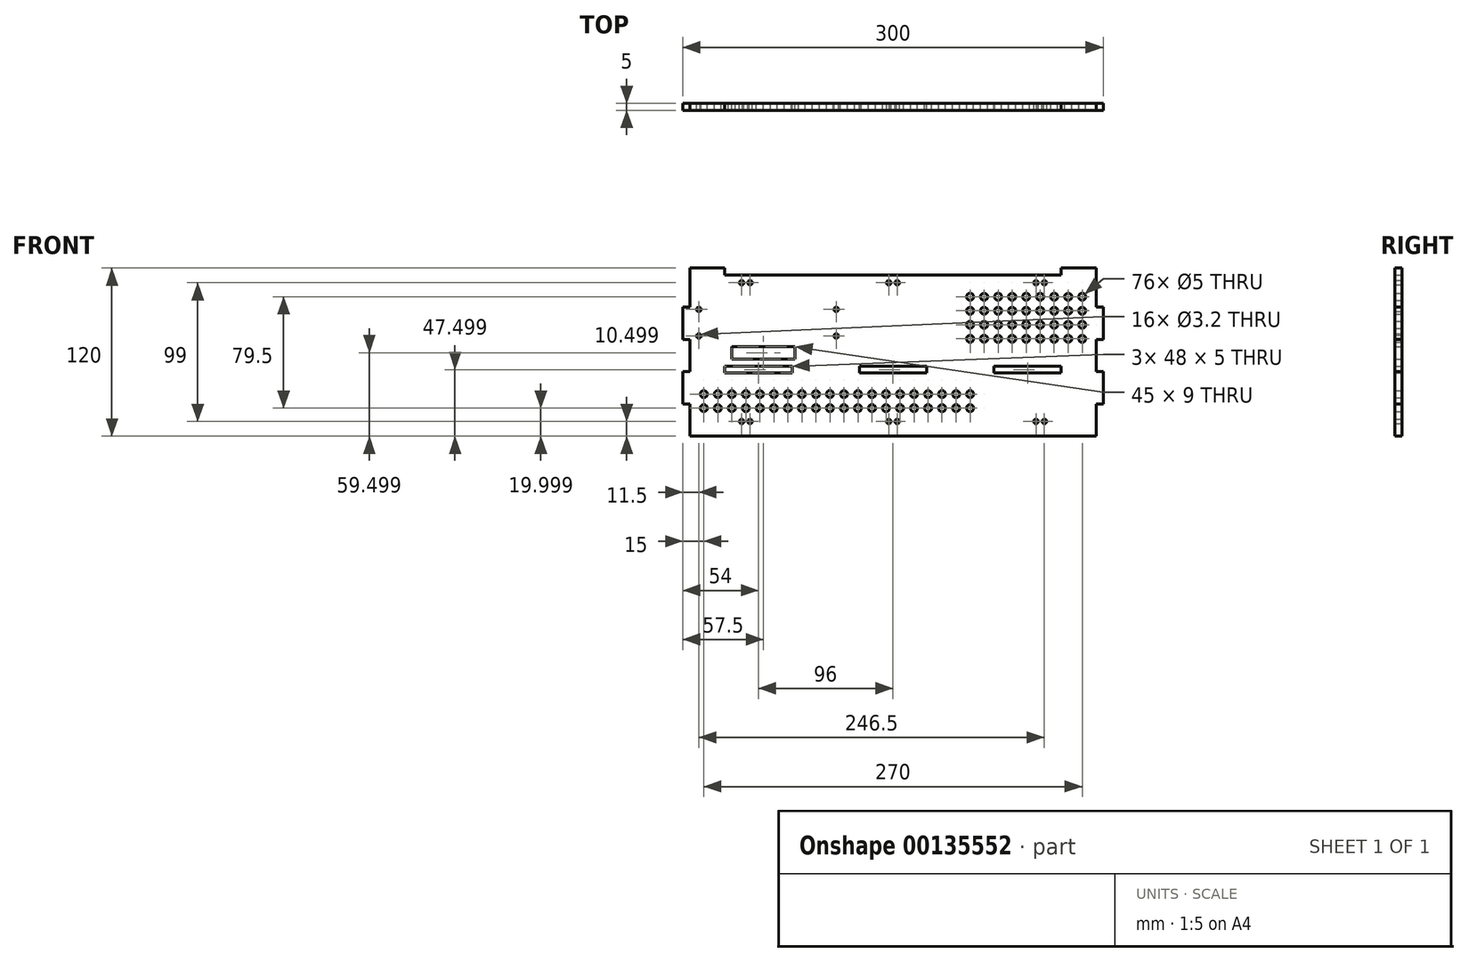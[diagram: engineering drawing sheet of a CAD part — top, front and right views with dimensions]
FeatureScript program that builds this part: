
annotation { "Feature Type Name" : "Feature", "Feature Type Description" : "" }
export const myFeature = defineFeature(function(context is Context, id is Id, definition is map)
    precondition{}
    {
        {
            var Q0;
            Q0=qCreatedBy(makeId("Front.planeOp"),FACE);
            var sketch = newSketch(context, id + "F0", { "sketchPlane" : qUnion([Q0])});
            skLineSegment(sketch, "E0", {"start": v(-150, -2.3) * mm, "end": v(150, -2.3) * mm, "construction": true});
            skLineSegment(sketch, "E1", {"start": v(0, 57.7) * mm, "end": v(0, -62.3) * mm, "construction": true});
            skLineSegment(sketch, "E2.bottom", {"start": v(145, -62.3) * mm, "end": v(-145, -62.3) * mm});
            skLineSegment(sketch, "E2.left", {"start": v(150, -39.3) * mm, "end": v(150, -16.3) * mm});
            skLineSegment(sketch, "E2.right", {"start": v(-150, -39.3) * mm, "end": v(-150, -12.3) * mm});
            skLineSegment(sketch, "E3", {"start": v(-166.62, -12.3) * mm, "end": v(178.21, -12.3) * mm, "construction": true});
            skLineSegment(sketch, "E4", {"start": v(165.43, -17.3) * mm, "end": v(-167.44, -17.3) * mm, "construction": true});
            skLineSegment(sketch, "E5", {"start": v(162.95, 52.7) * mm, "end": v(150, 52.7) * mm, "construction": true});
            skLineSegment(sketch, "E6", {"start": v(-120, 57.7) * mm, "end": v(-120, 52.7) * mm});
            skLineSegment(sketch, "E7", {"start": v(120, 57.7) * mm, "end": v(120, 52.7) * mm});
            skPoint(sketch, "E8.orphan", {"position": v(-150, 57.7) * mm});
            skLineSegment(sketch, "E9", {"start": v(145, 88.12) * mm, "end": v(145, -101.98) * mm, "construction": true});
            skLineSegment(sketch, "E10", {"start": v(-145, 88.12) * mm, "end": v(-145, -98.05) * mm, "construction": true});
            skLineSegment(sketch, "E11", {"start": v(120, 55.2) * mm, "end": v(120, -62.3) * mm, "construction": true});
            skLineSegment(sketch, "E12", {"start": v(-120, -62.3) * mm, "end": v(-120, 52.7) * mm, "construction": true});
            skLineSegment(sketch, "E13", {"start": v(105, 57.7) * mm, "end": v(105, -62.3) * mm, "construction": true});
            skLineSegment(sketch, "E14", {"start": v(-105, 57.7) * mm, "end": v(-105, -62.3) * mm, "construction": true});
            skLineSegment(sketch, "E15", {"start": v(150, 47.2) * mm, "end": v(-150, 47.2) * mm, "construction": true});
            skCircle(sketch, "E16", {"center": v(102, 47.2) * mm, "radius": 1.6 * mm});
            skCircle(sketch, "E17", {"center": v(108, 47.2) * mm, "radius": 1.6 * mm});
            skCircle(sketch, "E18", {"center": v(3, 47.2) * mm, "radius": 1.6 * mm});
            skCircle(sketch, "E19", {"center": v(-3, 47.2) * mm, "radius": 1.6 * mm});
            skCircle(sketch, "E20", {"center": v(-108, 47.2) * mm, "radius": 1.6 * mm});
            skCircle(sketch, "E21", {"center": v(-102, 47.2) * mm, "radius": 1.6 * mm});
            skLineSegment(sketch, "E22.bottom", {"start": v(-120, -12.3) * mm, "end": v(-72, -12.3) * mm});
            skLineSegment(sketch, "E22.top", {"start": v(-120, -17.3) * mm, "end": v(-72, -17.3) * mm});
            skLineSegment(sketch, "E22.left", {"start": v(-120, -12.3) * mm, "end": v(-120, -17.3) * mm});
            skLineSegment(sketch, "E22.right", {"start": v(-72, -12.3) * mm, "end": v(-72, -17.3) * mm});
            skLineSegment(sketch, "E23.bottom", {"start": v(-24, -12.3) * mm, "end": v(24, -12.3) * mm});
            skLineSegment(sketch, "E23.top", {"start": v(-24, -17.3) * mm, "end": v(24, -17.3) * mm});
            skLineSegment(sketch, "E23.left", {"start": v(-24, -12.3) * mm, "end": v(-24, -17.3) * mm});
            skLineSegment(sketch, "E23.right", {"start": v(24, -12.3) * mm, "end": v(24, -17.3) * mm});
            skLineSegment(sketch, "E24.bottom", {"start": v(72, -12.3) * mm, "end": v(120, -12.3) * mm});
            skLineSegment(sketch, "E24.top", {"start": v(72, -17.3) * mm, "end": v(120, -17.3) * mm});
            skLineSegment(sketch, "E24.left", {"start": v(72, -12.3) * mm, "end": v(72, -17.3) * mm});
            skLineSegment(sketch, "E24.right", {"start": v(120, -12.3) * mm, "end": v(120, -17.3) * mm});
            skLineSegment(sketch, "E25.bottom", {"start": v(-115, 1.7) * mm, "end": v(-70, 1.7) * mm});
            skLineSegment(sketch, "E25.top", {"start": v(-115, -7.3) * mm, "end": v(-70, -7.3) * mm});
            skLineSegment(sketch, "E25.left", {"start": v(-115, 1.7) * mm, "end": v(-115, -7.3) * mm});
            skLineSegment(sketch, "E25.right", {"start": v(-70, 1.7) * mm, "end": v(-70, -7.3) * mm});
            skCircle(sketch, "E26.MirrorC", {"center": v(-108, -51.8) * mm, "radius": 1.6 * mm});
            skCircle(sketch, "E27.MirrorC", {"center": v(-102, -51.8) * mm, "radius": 1.6 * mm});
            skCircle(sketch, "E28.MirrorC", {"center": v(108, -51.8) * mm, "radius": 1.6 * mm});
            skCircle(sketch, "E29.MirrorC", {"center": v(102, -51.8) * mm, "radius": 1.6 * mm});
            skCircle(sketch, "E30.MirrorC", {"center": v(3, -51.8) * mm, "radius": 1.6 * mm});
            skCircle(sketch, "E31.MirrorC", {"center": v(-3, -51.8) * mm, "radius": 1.6 * mm});
            skLineSegment(sketch, "E32", {"start": v(-145, -39.3) * mm, "end": v(-150, -39.3) * mm});
            skLineSegment(sketch, "E33.0.1.0", {"start": v(-145, -16.3) * mm, "end": v(-150, -16.3) * mm});
            skLineSegment(sketch, "E33.0.2.0", {"start": v(-145, 6.7) * mm, "end": v(-150, 6.7) * mm});
            skLineSegment(sketch, "E33.0.3.0", {"start": v(-145, 29.7) * mm, "end": v(-150, 29.7) * mm});
            skLineSegment(sketch, "E33.direction1", {"start": v(-150, -39.3) * mm, "end": v(-125, -39.3) * mm, "construction": true});
            skLineSegment(sketch, "E33.direction2", {"start": v(-150, -39.3) * mm, "end": v(-150, -16.3) * mm, "construction": true});
            skLineSegment(sketch, "E34", {"start": v(145, -39.3) * mm, "end": v(150, -39.3) * mm});
            skLineSegment(sketch, "E35.0.1.0", {"start": v(145, -16.3) * mm, "end": v(150, -16.3) * mm});
            skLineSegment(sketch, "E35.0.2.0", {"start": v(145, 6.7) * mm, "end": v(150, 6.7) * mm});
            skLineSegment(sketch, "E35.0.3.0", {"start": v(145, 29.7) * mm, "end": v(150, 29.7) * mm});
            skLineSegment(sketch, "E35.direction1", {"start": v(145, -39.3) * mm, "end": v(170, -39.3) * mm, "construction": true});
            skLineSegment(sketch, "E35.direction2", {"start": v(145, -39.3) * mm, "end": v(145, -16.3) * mm, "construction": true});
            skLineSegment(sketch, "E36", {"start": v(-145, -62.3) * mm, "end": v(-145, -39.3) * mm});
            skLineSegment(sketch, "E37", {"start": v(-145, 6.7) * mm, "end": v(-145, -16.3) * mm});
            skLineSegment(sketch, "E38", {"start": v(-145, 29.7) * mm, "end": v(-145, 52.7) * mm});
            skLineSegment(sketch, "E39.trimOffspring", {"start": v(-150, 52.7) * mm, "end": v(-172.8, 52.7) * mm, "construction": true});
            skPoint(sketch, "E40.orphan", {"position": v(-150, 52.7) * mm});
            skLineSegment(sketch, "E41.trimOffspring", {"start": v(-150, 6.7) * mm, "end": v(-150, 29.7) * mm});
            skLineSegment(sketch, "E42", {"start": v(145, -62.3) * mm, "end": v(145, -39.3) * mm});
            skLineSegment(sketch, "E43", {"start": v(145, 6.7) * mm, "end": v(145, -16.3) * mm});
            skLineSegment(sketch, "E44", {"start": v(145, 29.7) * mm, "end": v(145, 52.7) * mm});
            skLineSegment(sketch, "E45.trimOffspring", {"start": v(120, 52.7) * mm, "end": v(-120, 52.7) * mm, "construction": true});
            skLineSegment(sketch, "E46.trimOffspring", {"start": v(150, 6.7) * mm, "end": v(150, 29.7) * mm});
            skLineSegment(sketch, "E47", {"start": v(120, 57.7) * mm, "end": v(145, 57.7) * mm});
            skLineSegment(sketch, "E48", {"start": v(145, 57.7) * mm, "end": v(145, 52.7) * mm});
            skLineSegment(sketch, "E49", {"start": v(-120, 57.7) * mm, "end": v(-145, 57.7) * mm});
            skLineSegment(sketch, "E50", {"start": v(-145, 57.7) * mm, "end": v(-145, 52.7) * mm});
            skLineSegment(sketch, "E51", {"start": v(-120, 52.7) * mm, "end": v(120, 52.7) * mm});
            skSolve(sketch);
        }
        {
            var Q0;
            Q0=makeQuery(id+"F0.imprint","IMPRINT",FACE,{"disambiguationData":[TD([[makeQuery(id+"F0.imprint","IMPRINT",EDGE,{"derivedFrom":sQuery(id+"F0.wireOp",EDGE,"E2.bottom")}),-1.0]])]});
            var sketch = newSketch(context, id + "F1", { "sketchPlane" : qUnion([Q0])});
            skLineSegment(sketch, "E52.bottom", {"start": v(-144, 37.7) * mm, "end": v(-34, 37.7) * mm, "construction": true});
            skLineSegment(sketch, "E52.top", {"start": v(-144, 3.7) * mm, "end": v(-34, 3.7) * mm, "construction": true});
            skLineSegment(sketch, "E52.left", {"start": v(-144, 37.7) * mm, "end": v(-144, 3.7) * mm, "construction": true});
            skLineSegment(sketch, "E52.right", {"start": v(-34, 37.7) * mm, "end": v(-34, 3.7) * mm, "construction": true});
            skLineSegment(sketch, "E53.bottom", {"start": v(-138.5, 28.2) * mm, "end": v(-40.5, 28.2) * mm, "construction": true});
            skLineSegment(sketch, "E53.top", {"start": v(-138.5, 9.2) * mm, "end": v(-40.5, 9.2) * mm, "construction": true});
            skLineSegment(sketch, "E53.left", {"start": v(-138.5, 28.2) * mm, "end": v(-138.5, 9.2) * mm, "construction": true});
            skLineSegment(sketch, "E53.right", {"start": v(-40.5, 28.2) * mm, "end": v(-40.5, 9.2) * mm, "construction": true});
            skCircle(sketch, "E54", {"center": v(-138.5, 28.2) * mm, "radius": 1.6 * mm});
            skCircle(sketch, "E55", {"center": v(-138.5, 9.2) * mm, "radius": 1.6 * mm});
            skCircle(sketch, "E56", {"center": v(-40.5, 9.2) * mm, "radius": 1.6 * mm});
            skCircle(sketch, "E57", {"center": v(-40.5, 28.2) * mm, "radius": 1.6 * mm});
            skSolve(sketch);
        }
        {
            var Q0;
            Q0=makeQuery(id+"F0.imprint","IMPRINT",FACE,{"disambiguationData":[TD([[makeQuery(id+"F0.imprint","IMPRINT",EDGE,{"derivedFrom":sQuery(id+"F0.wireOp",EDGE,"E2.bottom")}),-1.0]])]});
            var sketch = newSketch(context, id + "F2", { "sketchPlane" : qUnion([Q0])});
            skCircle(sketch, "E58", {"center": v(135, 37.2) * mm, "radius": 2.5 * mm});
            skCircle(sketch, "E59.0.1.0", {"center": v(135, 27.2) * mm, "radius": 2.5 * mm});
            skCircle(sketch, "E59.0.2.0", {"center": v(135, 17.2) * mm, "radius": 2.5 * mm});
            skCircle(sketch, "E59.0.3.0", {"center": v(135, 7.2) * mm, "radius": 2.5 * mm});
            skCircle(sketch, "E59.1.0.0", {"center": v(125, 37.2) * mm, "radius": 2.5 * mm});
            skCircle(sketch, "E59.1.1.0", {"center": v(125, 27.2) * mm, "radius": 2.5 * mm});
            skCircle(sketch, "E59.1.2.0", {"center": v(125, 17.2) * mm, "radius": 2.5 * mm});
            skCircle(sketch, "E59.1.3.0", {"center": v(125, 7.2) * mm, "radius": 2.5 * mm});
            skCircle(sketch, "E59.2.0.0", {"center": v(115, 37.2) * mm, "radius": 2.5 * mm});
            skCircle(sketch, "E59.2.1.0", {"center": v(115, 27.2) * mm, "radius": 2.5 * mm});
            skCircle(sketch, "E59.2.2.0", {"center": v(115, 17.2) * mm, "radius": 2.5 * mm});
            skCircle(sketch, "E59.2.3.0", {"center": v(115, 7.2) * mm, "radius": 2.5 * mm});
            skCircle(sketch, "E59.3.0.0", {"center": v(105, 37.2) * mm, "radius": 2.5 * mm});
            skCircle(sketch, "E59.3.1.0", {"center": v(105, 27.2) * mm, "radius": 2.5 * mm});
            skCircle(sketch, "E59.3.2.0", {"center": v(105, 17.2) * mm, "radius": 2.5 * mm});
            skCircle(sketch, "E59.3.3.0", {"center": v(105, 7.2) * mm, "radius": 2.5 * mm});
            skCircle(sketch, "E59.4.0.0", {"center": v(95, 37.2) * mm, "radius": 2.5 * mm});
            skCircle(sketch, "E59.4.1.0", {"center": v(95, 27.2) * mm, "radius": 2.5 * mm});
            skCircle(sketch, "E59.4.2.0", {"center": v(95, 17.2) * mm, "radius": 2.5 * mm});
            skCircle(sketch, "E59.4.3.0", {"center": v(95, 7.2) * mm, "radius": 2.5 * mm});
            skCircle(sketch, "E59.5.0.0", {"center": v(85, 37.2) * mm, "radius": 2.5 * mm});
            skCircle(sketch, "E59.5.1.0", {"center": v(85, 27.2) * mm, "radius": 2.5 * mm});
            skCircle(sketch, "E59.5.2.0", {"center": v(85, 17.2) * mm, "radius": 2.5 * mm});
            skCircle(sketch, "E59.5.3.0", {"center": v(85, 7.2) * mm, "radius": 2.5 * mm});
            skCircle(sketch, "E59.6.0.0", {"center": v(75, 37.2) * mm, "radius": 2.5 * mm});
            skCircle(sketch, "E59.6.1.0", {"center": v(75, 27.2) * mm, "radius": 2.5 * mm});
            skCircle(sketch, "E59.6.2.0", {"center": v(75, 17.2) * mm, "radius": 2.5 * mm});
            skCircle(sketch, "E59.6.3.0", {"center": v(75, 7.2) * mm, "radius": 2.5 * mm});
            skCircle(sketch, "E59.7.0.0", {"center": v(65, 37.2) * mm, "radius": 2.5 * mm});
            skCircle(sketch, "E59.7.1.0", {"center": v(65, 27.2) * mm, "radius": 2.5 * mm});
            skCircle(sketch, "E59.7.2.0", {"center": v(65, 17.2) * mm, "radius": 2.5 * mm});
            skCircle(sketch, "E59.7.3.0", {"center": v(65, 7.2) * mm, "radius": 2.5 * mm});
            skCircle(sketch, "E59.8.0.0", {"center": v(55, 37.2) * mm, "radius": 2.5 * mm});
            skCircle(sketch, "E59.8.1.0", {"center": v(55, 27.2) * mm, "radius": 2.5 * mm});
            skCircle(sketch, "E59.8.2.0", {"center": v(55, 17.2) * mm, "radius": 2.5 * mm});
            skCircle(sketch, "E59.8.3.0", {"center": v(55, 7.2) * mm, "radius": 2.5 * mm});
            skLineSegment(sketch, "E59.direction1", {"start": v(135, 37.2) * mm, "end": v(125, 37.2) * mm, "construction": true});
            skLineSegment(sketch, "E59.direction2", {"start": v(135, 37.2) * mm, "end": v(135, 27.2) * mm, "construction": true});
            skCircle(sketch, "E60", {"center": v(-135, -42.3) * mm, "radius": 2.5 * mm});
            skCircle(sketch, "E61.0.1.0", {"center": v(-135, -32.3) * mm, "radius": 2.5 * mm});
            skCircle(sketch, "E61.1.0.0", {"center": v(-125, -42.3) * mm, "radius": 2.5 * mm});
            skCircle(sketch, "E61.1.1.0", {"center": v(-125, -32.3) * mm, "radius": 2.5 * mm});
            skCircle(sketch, "E61.2.0.0", {"center": v(-115, -42.3) * mm, "radius": 2.5 * mm});
            skCircle(sketch, "E61.2.1.0", {"center": v(-115, -32.3) * mm, "radius": 2.5 * mm});
            skCircle(sketch, "E61.3.0.0", {"center": v(-105, -42.3) * mm, "radius": 2.5 * mm});
            skCircle(sketch, "E61.3.1.0", {"center": v(-105, -32.3) * mm, "radius": 2.5 * mm});
            skCircle(sketch, "E61.4.0.0", {"center": v(-95, -42.3) * mm, "radius": 2.5 * mm});
            skCircle(sketch, "E61.4.1.0", {"center": v(-95, -32.3) * mm, "radius": 2.5 * mm});
            skCircle(sketch, "E61.5.0.0", {"center": v(-85, -42.3) * mm, "radius": 2.5 * mm});
            skCircle(sketch, "E61.5.1.0", {"center": v(-85, -32.3) * mm, "radius": 2.5 * mm});
            skCircle(sketch, "E61.6.0.0", {"center": v(-75, -42.3) * mm, "radius": 2.5 * mm});
            skCircle(sketch, "E61.6.1.0", {"center": v(-75, -32.3) * mm, "radius": 2.5 * mm});
            skCircle(sketch, "E61.7.0.0", {"center": v(-65, -42.3) * mm, "radius": 2.5 * mm});
            skCircle(sketch, "E61.7.1.0", {"center": v(-65, -32.3) * mm, "radius": 2.5 * mm});
            skCircle(sketch, "E61.8.0.0", {"center": v(-55, -42.3) * mm, "radius": 2.5 * mm});
            skCircle(sketch, "E61.8.1.0", {"center": v(-55, -32.3) * mm, "radius": 2.5 * mm});
            skCircle(sketch, "E61.9.0.0", {"center": v(-45, -42.3) * mm, "radius": 2.5 * mm});
            skCircle(sketch, "E61.9.1.0", {"center": v(-45, -32.3) * mm, "radius": 2.5 * mm});
            skCircle(sketch, "E61.10.0.0", {"center": v(-35, -42.3) * mm, "radius": 2.5 * mm});
            skCircle(sketch, "E61.10.1.0", {"center": v(-35, -32.3) * mm, "radius": 2.5 * mm});
            skCircle(sketch, "E61.11.0.0", {"center": v(-25, -42.3) * mm, "radius": 2.5 * mm});
            skCircle(sketch, "E61.11.1.0", {"center": v(-25, -32.3) * mm, "radius": 2.5 * mm});
            skCircle(sketch, "E61.12.0.0", {"center": v(-15, -42.3) * mm, "radius": 2.5 * mm});
            skCircle(sketch, "E61.12.1.0", {"center": v(-15, -32.3) * mm, "radius": 2.5 * mm});
            skCircle(sketch, "E61.13.0.0", {"center": v(-5, -42.3) * mm, "radius": 2.5 * mm});
            skCircle(sketch, "E61.13.1.0", {"center": v(-5, -32.3) * mm, "radius": 2.5 * mm});
            skCircle(sketch, "E61.14.0.0", {"center": v(5, -42.3) * mm, "radius": 2.5 * mm});
            skCircle(sketch, "E61.14.1.0", {"center": v(5, -32.3) * mm, "radius": 2.5 * mm});
            skCircle(sketch, "E61.15.0.0", {"center": v(15, -42.3) * mm, "radius": 2.5 * mm});
            skCircle(sketch, "E61.15.1.0", {"center": v(15, -32.3) * mm, "radius": 2.5 * mm});
            skCircle(sketch, "E61.16.0.0", {"center": v(25, -42.3) * mm, "radius": 2.5 * mm});
            skCircle(sketch, "E61.16.1.0", {"center": v(25, -32.3) * mm, "radius": 2.5 * mm});
            skCircle(sketch, "E61.17.0.0", {"center": v(35, -42.3) * mm, "radius": 2.5 * mm});
            skCircle(sketch, "E61.17.1.0", {"center": v(35, -32.3) * mm, "radius": 2.5 * mm});
            skCircle(sketch, "E61.18.0.0", {"center": v(45, -42.3) * mm, "radius": 2.5 * mm});
            skCircle(sketch, "E61.18.1.0", {"center": v(45, -32.3) * mm, "radius": 2.5 * mm});
            skCircle(sketch, "E61.19.0.0", {"center": v(55, -42.3) * mm, "radius": 2.5 * mm});
            skCircle(sketch, "E61.19.1.0", {"center": v(55, -32.3) * mm, "radius": 2.5 * mm});
            skLineSegment(sketch, "E61.direction1", {"start": v(-135, -42.3) * mm, "end": v(-125, -42.3) * mm, "construction": true});
            skLineSegment(sketch, "E61.direction2", {"start": v(-135, -42.3) * mm, "end": v(-135, -32.3) * mm, "construction": true});
            skSolve(sketch);
        }
        {
            var Q0;
            Q0 = qSketchRegion(id + "F0", true);
            extrude(context, id + "F3", {"entities" : qUnion([Q0]), "depth" : 5 * mm});
        }
        {
            var Q0;
            Q0 = qSketchRegion(id + "F1", true);
            var Q1;
            Q1 = qSketchRegion(id + "F2", true);
            extrude(context, id + "F4", {"entities" : qUnion([Q0, Q1]), "operationType" : NewBodyOperationType.REMOVE, "depth" : 5 * mm});
        }
    });
